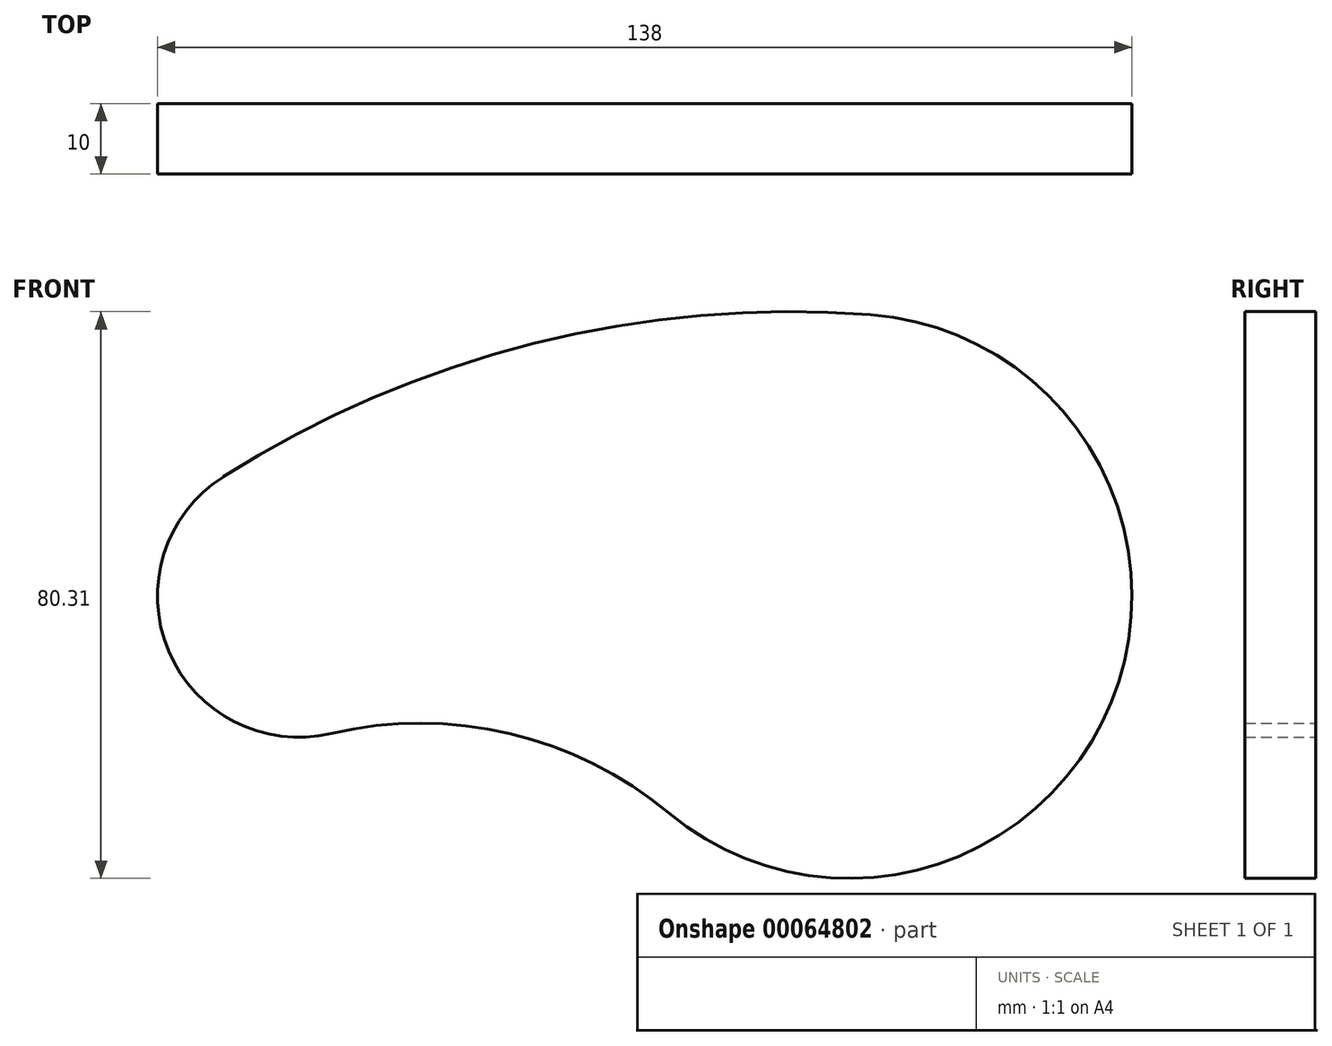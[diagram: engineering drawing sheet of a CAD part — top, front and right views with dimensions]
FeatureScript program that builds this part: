
annotation { "Feature Type Name" : "Feature", "Feature Type Description" : "" }
export const myFeature = defineFeature(function(context is Context, id is Id, definition is map)
    precondition{}
    {
        {
            var Q0;
            Q0=qCreatedBy(makeId("Front.planeOp"),FACE);
            var sketch = newSketch(context, id + "F0", { "sketchPlane" : qUnion([Q0])});
            skArc(sketch, "E0", {"start": v(-25.6, -30.74) * mm, "mid": v(37.08, -15) * mm, "end": v(3, 39.89) * mm});
            skArc(sketch, "E1", {"start": v(-88.73, 16.88) * mm, "mid": v(-96.43, -7.77) * mm, "end": v(-73.41, -19.47) * mm});
            skArc(sketch, "E2", {"start": v(3, 39.89) * mm, "mid": v(-44.73, 35.8) * mm, "end": v(-88.73, 16.88) * mm});
            skArc(sketch, "E3", {"start": v(-25.6, -30.74) * mm, "mid": v(-48.18, -19.47) * mm, "end": v(-73.41, -19.47) * mm});
            skSolve(sketch);
        }
        {
            var Q0;
            Q0=makeQuery(id+"F0.imprint","IMPRINT",FACE,{"disambiguationData":[TD([[makeQuery(id+"F0.imprint","IMPRINT",EDGE,{"derivedFrom":sQuery(id+"F0.wireOp",EDGE,"E0")}),1.0]])]});
            extrude(context, id + "F1", {"entities" : qUnion([Q0]), "flatOperationType" : FlatOperationType.REMOVE, "offsetDistance" : 25 * mm, "depth" : 10 * mm, "domain" : OperationDomain.MODEL});
        }
    });
